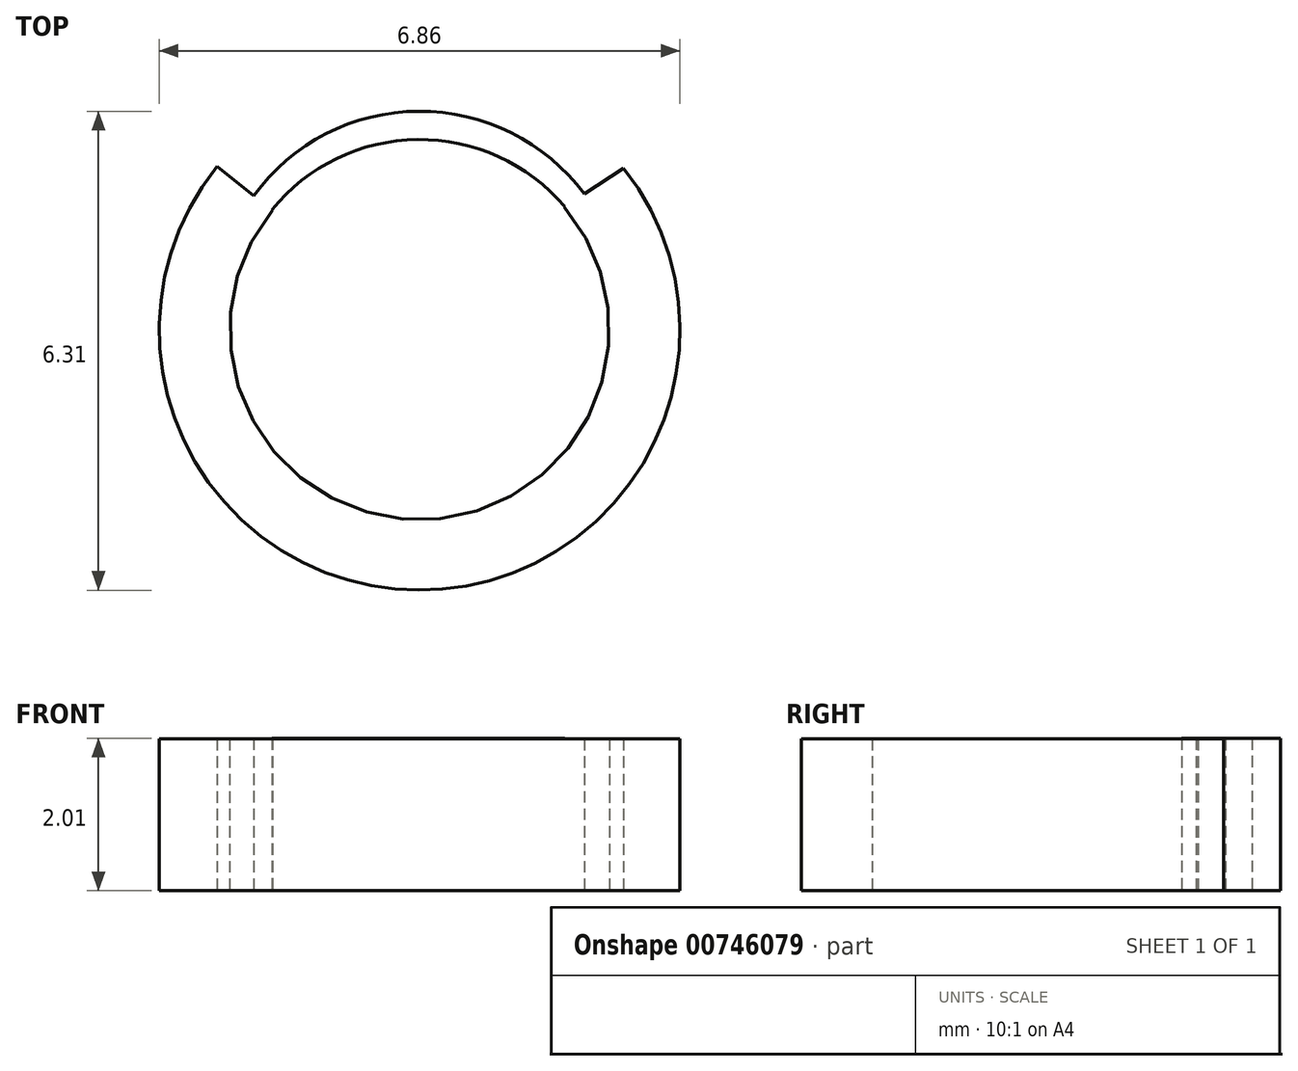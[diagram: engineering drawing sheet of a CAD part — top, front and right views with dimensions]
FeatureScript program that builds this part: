
annotation { "Feature Type Name" : "Feature", "Feature Type Description" : "" }
export const myFeature = defineFeature(function(context is Context, id is Id, definition is map)
    precondition{}
    {
        {
            var Q0;
            Q0=qCreatedBy(makeId("Top.planeOp"),FACE);
            var sketch = newSketch(context, id + "F0", { "sketchPlane" : qUnion([Q0])});
            skCircle(sketch, "E0", {"center": v(0, 0) * mm, "radius": 3.43 * mm});
            skSolve(sketch);
        }
        {
            var Q0;
            Q0=makeQuery(id+"F0.imprint","IMPRINT",FACE,{"disambiguationData":[TD([[makeQuery(id+"F0.imprint","IMPRINT",EDGE,{"derivedFrom":sQuery(id+"F0.wireOp",EDGE,"E0")}),1.0]])]});
            extrude(context, id + "F1", {"entities" : qUnion([Q0]), "depth" : 2 * mm, "offsetDistance" : 25.4 * mm});
        }
        {
            var Q0;
            Q0=makeQuery(id+"F1.opExtrude","CAP_FACE",FACE,{"disambiguationData":[OSD([sQuery(id+"F0.wireOp",EDGE,"E0")])],"isStart":true});
            var sketch = newSketch(context, id + "F2", { "sketchPlane" : qUnion([Q0])});
            skCircle(sketch, "E1", {"center": v(0, 0) * mm, "radius": 2.5 * mm});
            skSolve(sketch);
        }
        {
            var Q0;
            Q0 = qSketchRegion(id + "F2", true);
            extrude(context, id + "F3", {"entities" : qUnion([Q0]), "operationType" : NewBodyOperationType.REMOVE, "oppositeDirection" : true, "depth" : 25.4 * mm, "offsetDistance" : 25.4 * mm});
        }
        {
            var Q0;
            Q0=qCreatedBy(makeId("Top.planeOp"),FACE);
            var sketch = newSketch(context, id + "F4", { "sketchPlane" : qUnion([Q0])});
            skLineSegment(sketch, "E2", {"start": v(-2.7, 2.18) * mm, "end": v(-1.83, 1.49) * mm});
            skLineSegment(sketch, "E3", {"start": v(-1.83, 1.49) * mm, "end": v(1.7, 1.49) * mm});
            skLineSegment(sketch, "E4", {"start": v(1.7, 1.49) * mm, "end": v(2.76, 2.18) * mm});
            skLineSegment(sketch, "E5", {"start": v(2.76, 2.18) * mm, "end": v(-2.7, 2.18) * mm});
            skLineSegment(sketch, "E6", {"start": v(-2.7, 2.18) * mm, "end": v(-2.14, 3.06) * mm});
            skLineSegment(sketch, "E7", {"start": v(-2.14, 3.06) * mm, "end": v(-0.49, 3.6) * mm});
            skLineSegment(sketch, "E8", {"start": v(-0.49, 3.6) * mm, "end": v(1.82, 3.3) * mm});
            skLineSegment(sketch, "E9", {"start": v(1.82, 3.3) * mm, "end": v(2.76, 2.18) * mm});
            skSolve(sketch);
        }
        {
            var Q0;
            Q0=makeQuery(id+"F4.imprint","IMPRINT",FACE,{"disambiguationData":[TD([[makeQuery(id+"F4.imprint","IMPRINT",EDGE,{"derivedFrom":sQuery(id+"F4.wireOp",EDGE,"E2")}),1.0]])]});
            var Q1;
            Q1=makeQuery(id+"F4.imprint","IMPRINT",FACE,{"disambiguationData":[TD([[makeQuery(id+"F4.imprint","IMPRINT",EDGE,{"derivedFrom":sQuery(id+"F4.wireOp",EDGE,"E5")}),-1.0]])]});
            extrude(context, id + "F5", {"entities" : qUnion([Q0, Q1]), "operationType" : NewBodyOperationType.REMOVE, "oppositeDirection" : true, "depth" : -25.4 * mm, "offsetDistance" : 25.4 * mm});
        }
        {
            var Q0;
            Q0=qCreatedBy(makeId("Top.planeOp"),FACE);
            var sketch = newSketch(context, id + "F6", { "sketchPlane" : qUnion([Q0])});
            skCircle(sketch, "E10", {"center": v(0, 0) * mm, "radius": 2.5 * mm});
            skCircle(sketch, "E11", {"center": v(0, 0.18) * mm, "radius": 2.7 * mm});
            skSolve(sketch);
        }
        {
            var Q0;
            Q0=makeQuery(id+"F6.imprint","IMPRINT",FACE,{"disambiguationData":[TD([[makeQuery(id+"F6.imprint","IMPRINT",EDGE,{"derivedFrom":sQuery(id+"F6.wireOp",EDGE,"E10")}),-1.0]])]});
            extrude(context, id + "F7", {"entities" : qUnion([Q0]), "operationType" : NewBodyOperationType.ADD, "depth" : 2 * mm, "offsetDistance" : 25.4 * mm});
        }
    });
